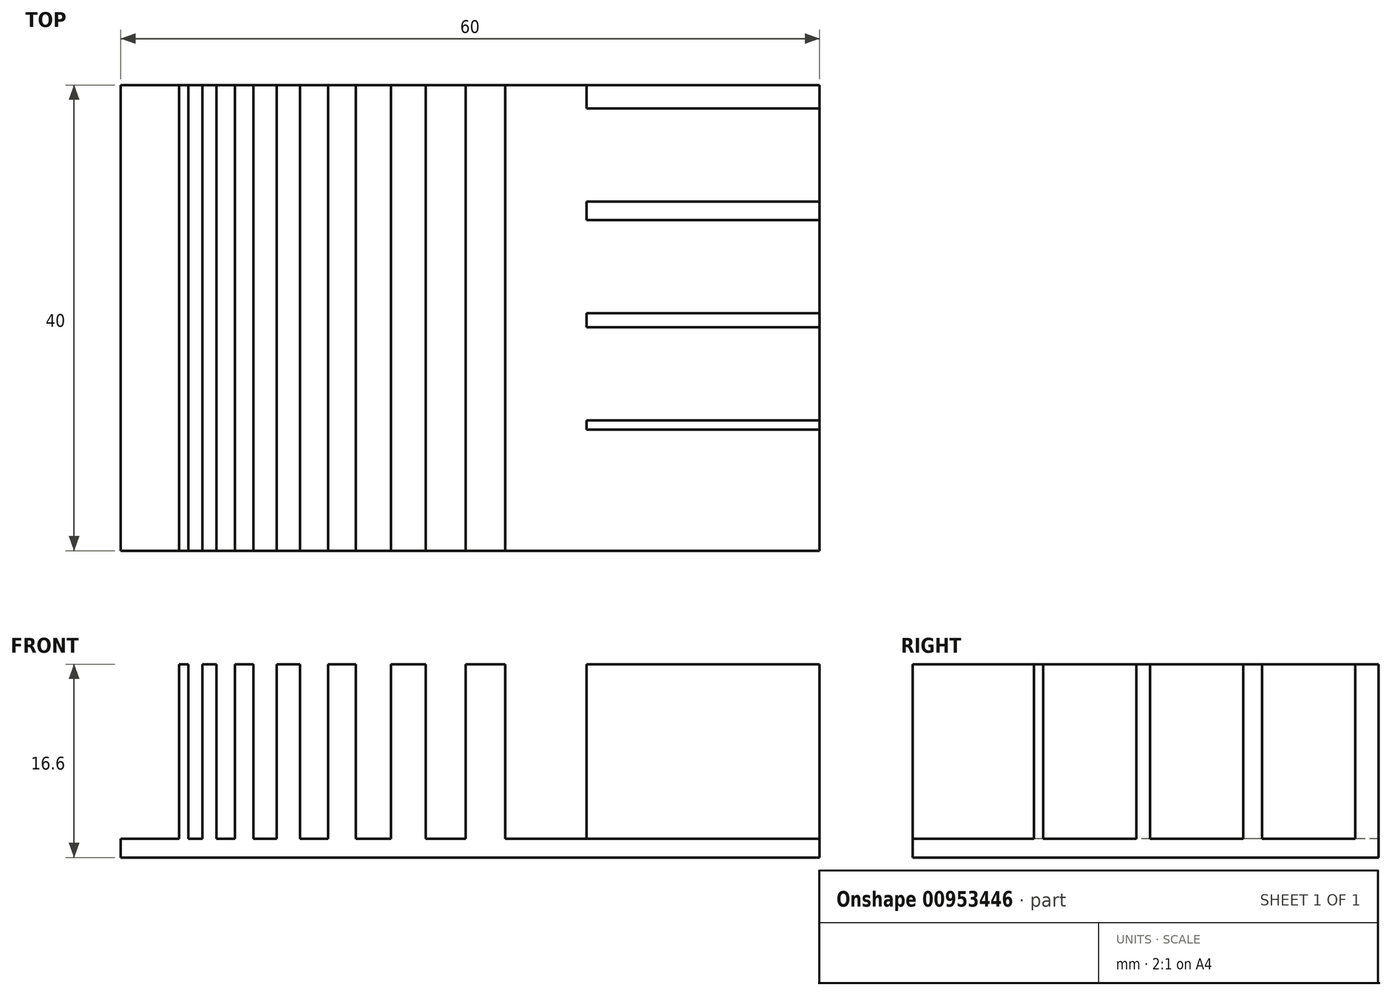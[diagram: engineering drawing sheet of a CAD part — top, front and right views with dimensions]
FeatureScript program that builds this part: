
annotation { "Feature Type Name" : "Feature", "Feature Type Description" : "" }
export const myFeature = defineFeature(function(context is Context, id is Id, definition is map)
    precondition{}
    {
        {
            var Q0;
            Q0=qCreatedBy(makeId("Top.planeOp"),FACE);
            var sketch = newSketch(context, id + "F0", { "sketchPlane" : qUnion([Q0])});
            skLineSegment(sketch, "E0.bottom", {"start": v(0, 0) * mm, "end": v(60, 0) * mm});
            skLineSegment(sketch, "E0.top", {"start": v(0, -40) * mm, "end": v(60, -40) * mm});
            skLineSegment(sketch, "E0.left", {"start": v(0, 0) * mm, "end": v(0, -40) * mm});
            skLineSegment(sketch, "E0.right", {"start": v(60, 0) * mm, "end": v(60, -40) * mm});
            skSolve(sketch);
        }
        {
            var Q0;
            Q0=makeQuery(id+"F0.imprint","IMPRINT",FACE,{"disambiguationData":[TD([[makeQuery(id+"F0.imprint","IMPRINT",EDGE,{"derivedFrom":sQuery(id+"F0.wireOp",EDGE,"E0.bottom")}),-1.0]])]});
            extrude(context, id + "F1", {"entities" : qUnion([Q0]), "depth" : 1.6 * mm, "offsetDistance" : 25 * mm});
        }
        {
            var Q0;
            Q0=makeQuery(id+"F1.opExtrude","CAP_FACE",FACE,{"disambiguationData":[OSD([sQuery(id+"F0.wireOp",EDGE,"E0.bottom"),sQuery(id+"F0.wireOp",EDGE,"E0.top"),sQuery(id+"F0.wireOp",EDGE,"E0.left"),sQuery(id+"F0.wireOp",EDGE,"E0.right")])],"isStart":false});
            var sketch = newSketch(context, id + "F2", { "sketchPlane" : qUnion([Q0])});
            skLineSegment(sketch, "E1.bottom", {"start": v(0, 0) * mm, "end": v(5, 0) * mm});
            skLineSegment(sketch, "E1.top", {"start": v(0, -40) * mm, "end": v(5, -40) * mm});
            skLineSegment(sketch, "E1.left", {"start": v(0, 0) * mm, "end": v(0, -40) * mm});
            skLineSegment(sketch, "E1.right", {"start": v(5, 0) * mm, "end": v(5, -40) * mm});
            skLineSegment(sketch, "E2.0", {"start": v(5.8, 0) * mm, "end": v(5.8, -40) * mm});
            skLineSegment(sketch, "E3.0", {"start": v(7, 0) * mm, "end": v(7, -40) * mm});
            skLineSegment(sketch, "E4.0", {"start": v(8.2, 0) * mm, "end": v(8.2, -40) * mm});
            skLineSegment(sketch, "E5.0", {"start": v(9.8, 0) * mm, "end": v(9.8, -40) * mm});
            skLineSegment(sketch, "E6.0", {"start": v(11.4, 0) * mm, "end": v(11.4, -40) * mm});
            skLineSegment(sketch, "E7.0", {"start": v(13.4, 0) * mm, "end": v(13.4, -40) * mm});
            skLineSegment(sketch, "E8.0", {"start": v(15.4, 0) * mm, "end": v(15.4, -40) * mm});
            skLineSegment(sketch, "E9.0", {"start": v(17.8, 0) * mm, "end": v(17.8, -40) * mm});
            skLineSegment(sketch, "E10.0", {"start": v(20.2, 0) * mm, "end": v(20.2, -40) * mm});
            skLineSegment(sketch, "E11.0", {"start": v(23.2, 0) * mm, "end": v(23.2, -40) * mm});
            skLineSegment(sketch, "E12.0", {"start": v(26.2, 0) * mm, "end": v(26.2, -40) * mm});
            skLineSegment(sketch, "E13.0", {"start": v(29.6, 0) * mm, "end": v(29.6, -40) * mm});
            skLineSegment(sketch, "E14.0", {"start": v(33, 0) * mm, "end": v(33, -40) * mm});
            skLineSegment(sketch, "E15.bottom", {"start": v(5, 0) * mm, "end": v(60, 0) * mm});
            skLineSegment(sketch, "E15.top", {"start": v(5, -40) * mm, "end": v(60, -40) * mm});
            skLineSegment(sketch, "E15.right", {"start": v(60, 0) * mm, "end": v(60, -40) * mm});
            skLineSegment(sketch, "E16.bottom", {"start": v(60, 0) * mm, "end": v(40, 0) * mm});
            skLineSegment(sketch, "E16.top", {"start": v(60, -2) * mm, "end": v(40, -2) * mm});
            skLineSegment(sketch, "E16.left", {"start": v(60, 0) * mm, "end": v(60, -2) * mm});
            skLineSegment(sketch, "E16.right", {"start": v(40, 0) * mm, "end": v(40, -2) * mm});
            skLineSegment(sketch, "E17.0", {"start": v(60, -10) * mm, "end": v(40, -10) * mm});
            skLineSegment(sketch, "E18.0", {"start": v(60, -11.6) * mm, "end": v(40, -11.6) * mm});
            skLineSegment(sketch, "E19.0", {"start": v(60, -19.6) * mm, "end": v(40, -19.6) * mm});
            skLineSegment(sketch, "E20.0", {"start": v(60, -20.8) * mm, "end": v(40, -20.8) * mm});
            skLineSegment(sketch, "E21.0", {"start": v(60, -28.8) * mm, "end": v(40, -28.8) * mm});
            skLineSegment(sketch, "E22.0", {"start": v(60, -29.6) * mm, "end": v(40, -29.6) * mm});
            skLineSegment(sketch, "E23", {"start": v(40, -10) * mm, "end": v(40, -29.6) * mm});
            skSolve(sketch);
        }
        {
            var Q0;
            {var subQ0=sQuery(id+"F2.wireOp",EDGE,"E1.right");Q0=makeQuery(id+"F2.imprint","IMPRINT",FACE,{"disambiguationData":[TD([[makeQuery(id+"F2.imprint","IMPRINT",EDGE,{"derivedFrom":subQ0}),1.0]])]});}
            var Q1;
            {var subQ0=sQuery(id+"F2.wireOp",EDGE,"E3.0");Q1=makeQuery(id+"F2.imprint","IMPRINT",FACE,{"disambiguationData":[TD([[makeQuery(id+"F2.imprint","IMPRINT",EDGE,{"derivedFrom":subQ0}),1.0]])]});}
            var Q2;
            {var subQ0=sQuery(id+"F2.wireOp",EDGE,"E5.0");Q2=makeQuery(id+"F2.imprint","IMPRINT",FACE,{"disambiguationData":[TD([[makeQuery(id+"F2.imprint","IMPRINT",EDGE,{"derivedFrom":subQ0}),1.0]])]});}
            var Q3;
            {var subQ0=sQuery(id+"F2.wireOp",EDGE,"E7.0");Q3=makeQuery(id+"F2.imprint","IMPRINT",FACE,{"disambiguationData":[TD([[makeQuery(id+"F2.imprint","IMPRINT",EDGE,{"derivedFrom":subQ0}),1.0]])]});}
            var Q4;
            {var subQ0=sQuery(id+"F2.wireOp",EDGE,"E9.0");Q4=makeQuery(id+"F2.imprint","IMPRINT",FACE,{"disambiguationData":[TD([[makeQuery(id+"F2.imprint","IMPRINT",EDGE,{"derivedFrom":subQ0}),1.0]])]});}
            var Q5;
            {var subQ0=sQuery(id+"F2.wireOp",EDGE,"E11.0");Q5=makeQuery(id+"F2.imprint","IMPRINT",FACE,{"disambiguationData":[TD([[makeQuery(id+"F2.imprint","IMPRINT",EDGE,{"derivedFrom":subQ0}),1.0]])]});}
            var Q6;
            {var subQ0=sQuery(id+"F2.wireOp",EDGE,"E13.0");Q6=makeQuery(id+"F2.imprint","IMPRINT",FACE,{"disambiguationData":[TD([[makeQuery(id+"F2.imprint","IMPRINT",EDGE,{"derivedFrom":subQ0}),1.0]])]});}
            var Q7;
            {var subQ0=sQuery(id+"F2.wireOp",EDGE,"E21.0");Q7=makeQuery(id+"F2.imprint","IMPRINT",FACE,{"disambiguationData":[TD([[makeQuery(id+"F2.imprint","IMPRINT",EDGE,{"derivedFrom":subQ0}),1.0]])]});}
            var Q8;
            {var subQ0=sQuery(id+"F2.wireOp",EDGE,"E19.0");Q8=makeQuery(id+"F2.imprint","IMPRINT",FACE,{"disambiguationData":[TD([[makeQuery(id+"F2.imprint","IMPRINT",EDGE,{"derivedFrom":subQ0}),1.0]])]});}
            var Q9;
            {var subQ0=sQuery(id+"F2.wireOp",EDGE,"E17.0");Q9=makeQuery(id+"F2.imprint","IMPRINT",FACE,{"disambiguationData":[TD([[makeQuery(id+"F2.imprint","IMPRINT",EDGE,{"derivedFrom":subQ0}),1.0]])]});}
            var Q10;
            {var subQ4=sQuery(id+"F2.wireOp",EDGE,"E16.top");Q10=makeQuery(id+"F2.imprint","IMPRINT",FACE,{"disambiguationData":[TD([[makeQuery(id+"F2.imprint","IMPRINT",EDGE,{"derivedFrom":subQ4}),-1.0]])]});}
            extrude(context, id + "F3", {"entities" : qUnion([Q0, Q1, Q2, Q3, Q4, Q5, Q6, Q7, Q8, Q9, Q10]), "operationType" : NewBodyOperationType.ADD, "depth" : 15 * mm, "offsetDistance" : 25 * mm});
        }
    });
